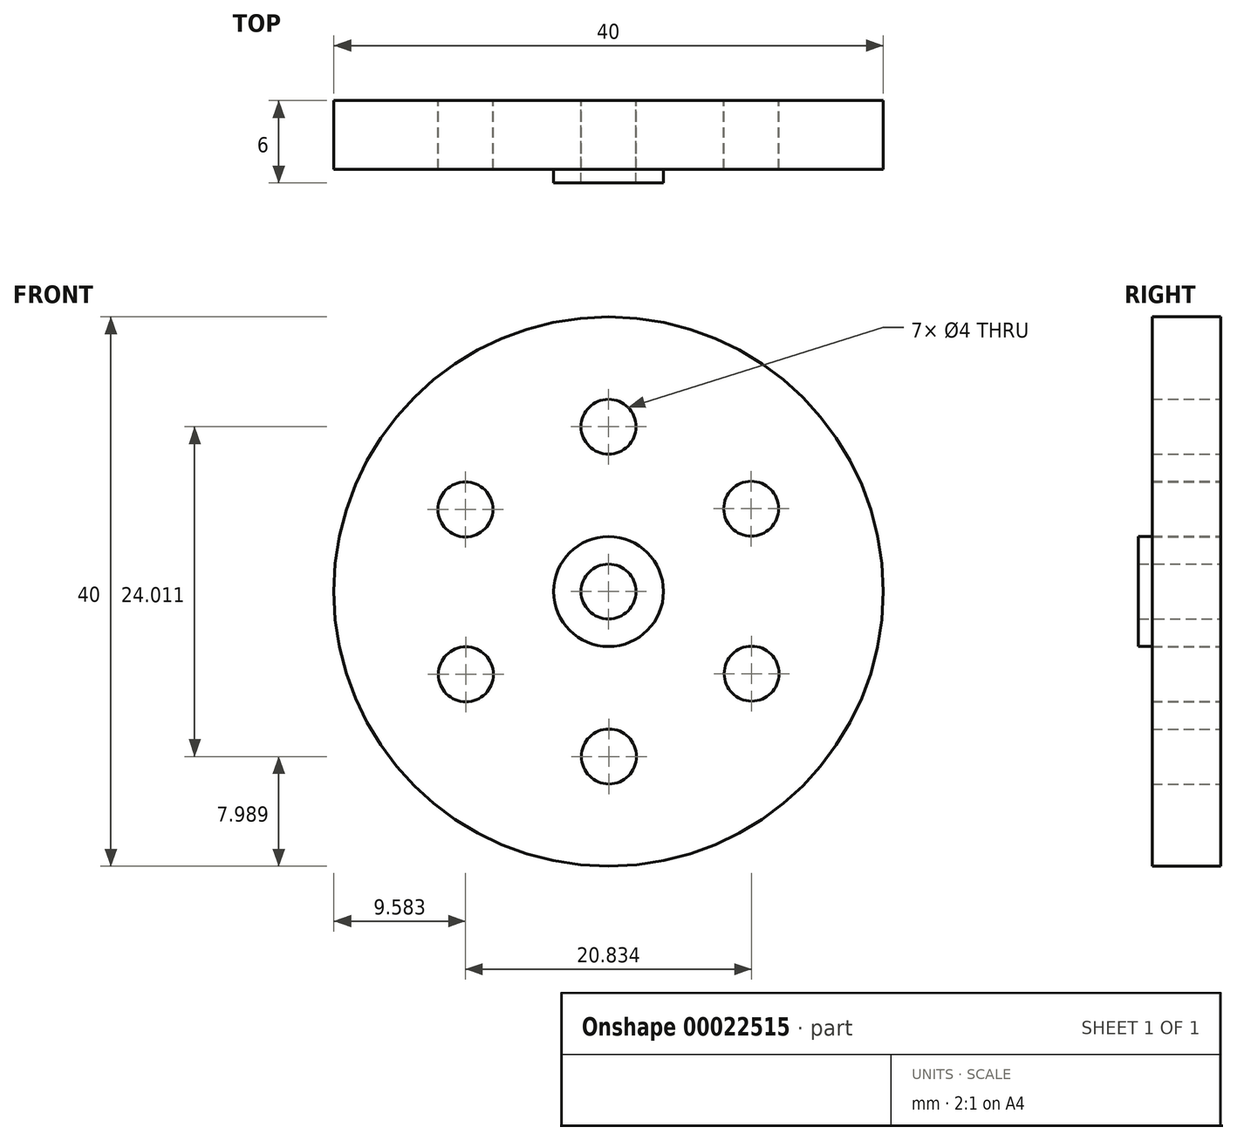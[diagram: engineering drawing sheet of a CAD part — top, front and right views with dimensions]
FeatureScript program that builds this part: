
annotation { "Feature Type Name" : "Feature", "Feature Type Description" : "" }
export const myFeature = defineFeature(function(context is Context, id is Id, definition is map)
    precondition{}
    {
        {
            var Q0;
            Q0=qCreatedBy(makeId("Front.planeOp"),FACE);
            var sketch = newSketch(context, id + "F0", { "sketchPlane" : qUnion([Q0])});
            skCircle(sketch, "E0", {"center": v(0, 0) * mm, "radius": 20 * mm});
            skCircle(sketch, "E1", {"center": v(0, 0) * mm, "radius": 4 * mm});
            skLineSegment(sketch, "E2", {"start": v(0, 0) * mm, "end": v(0, 12) * mm});
            skCircle(sketch, "E3.cCircle", {"center": v(0, 0) * mm, "radius": 10.4 * mm, "construction": true});
            skLineSegment(sketch, "E3.0", {"start": v(10.42, -5.98) * mm, "end": v(0.03, -12.01) * mm});
            skLineSegment(sketch, "E3.1", {"start": v(0.03, -12.01) * mm, "end": v(-10.39, -6.03) * mm});
            skLineSegment(sketch, "E3.2", {"start": v(-10.39, -6.03) * mm, "end": v(-10.42, 5.98) * mm});
            skLineSegment(sketch, "E3.3", {"start": v(-10.42, 5.98) * mm, "end": v(-0.03, 12.01) * mm});
            skLineSegment(sketch, "E3.4", {"start": v(-0.03, 12.01) * mm, "end": v(10.39, 6.03) * mm});
            skLineSegment(sketch, "E3.5", {"start": v(10.39, 6.03) * mm, "end": v(10.42, -5.98) * mm});
            skPoint(sketch, "E3.0.midPoint", {"position": v(5.22, -9) * mm});
            skCircle(sketch, "E4", {"center": v(-10.42, 5.98) * mm, "radius": 2 * mm});
            skCircle(sketch, "E5", {"center": v(0, 12) * mm, "radius": 2 * mm});
            skCircle(sketch, "E6", {"center": v(10.39, 6.03) * mm, "radius": 2 * mm});
            skCircle(sketch, "E7", {"center": v(10.42, -5.98) * mm, "radius": 2 * mm});
            skCircle(sketch, "E8", {"center": v(0.03, -12.01) * mm, "radius": 2 * mm});
            skCircle(sketch, "E9", {"center": v(-10.39, -6.03) * mm, "radius": 2 * mm});
            skCircle(sketch, "E10", {"center": v(0, 0) * mm, "radius": 2 * mm});
            skSolve(sketch);
        }
        {
            var Q0;
            Q0=makeQuery(id+"F0.imprint","IMPRINT",FACE,{"disambiguationData":[TD([[makeQuery(id+"F0.imprint","IMPRINT",EDGE,{"derivedFrom":sQuery(id+"F0.wireOp",EDGE,"E0")}),1.0]])]});
            var Q1;
            Q1=makeQuery(id+"F0.imprint","IMPRINT",FACE,{"disambiguationData":[TD([[makeQuery(id+"F0.imprint","IMPRINT",EDGE,{"derivedFrom":sQuery(id+"F0.wireOp",EDGE,"E1")}),-1.0]])]});
            extrude(context, id + "F1", {"entities" : qUnion([Q0, Q1]), "depth" : 5 * mm});
        }
        {
            var Q0;
            Q0=makeQuery(id+"F0.imprint","IMPRINT",FACE,{"disambiguationData":[TD([[makeQuery(id+"F0.imprint","IMPRINT",EDGE,{"derivedFrom":sQuery(id+"F0.wireOp",EDGE,"E1")}),1.0]])]});
            extrude(context, id + "F2", {"entities" : qUnion([Q0]), "operationType" : NewBodyOperationType.ADD, "depth" : 6 * mm});
        }
    });
